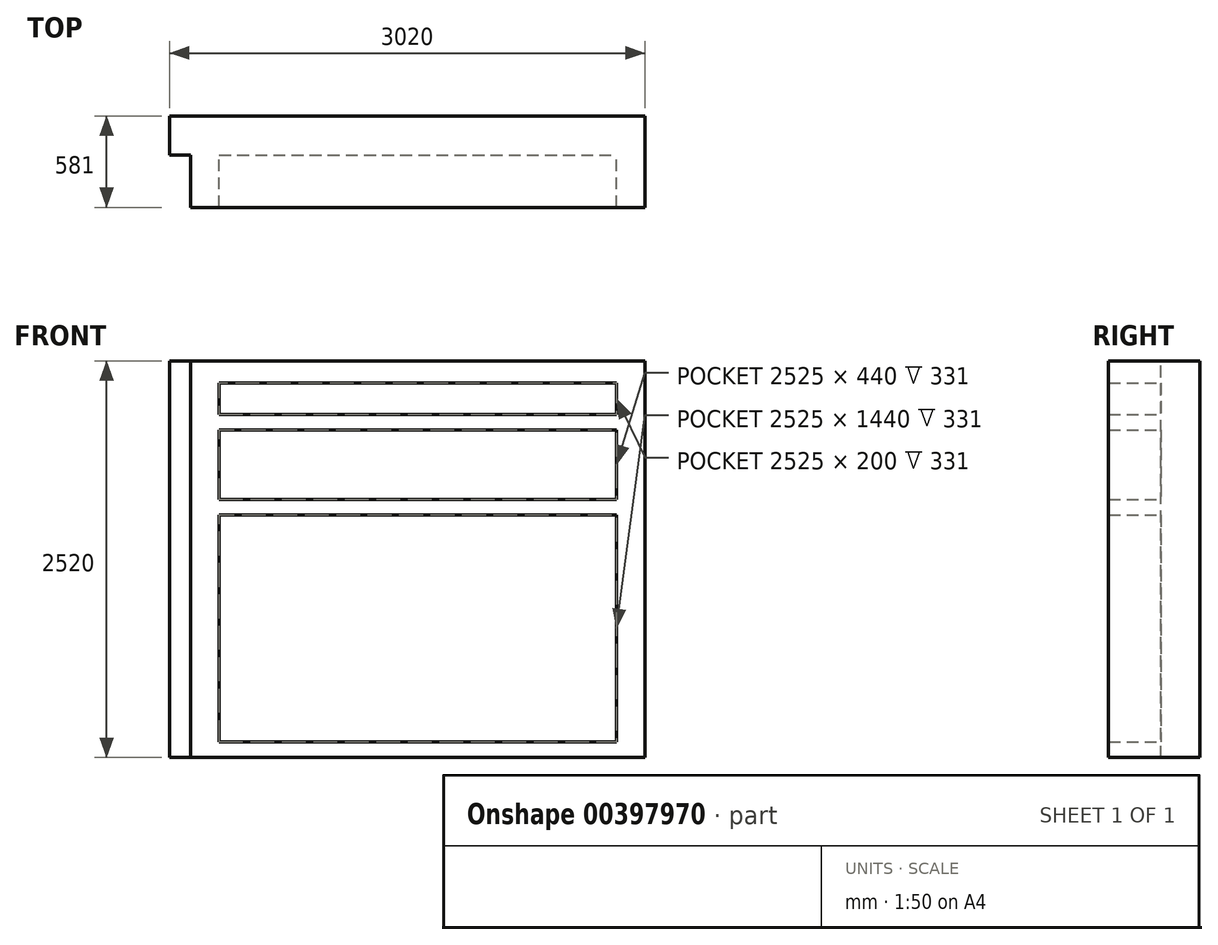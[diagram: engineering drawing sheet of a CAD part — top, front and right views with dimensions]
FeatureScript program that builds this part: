
annotation { "Feature Type Name" : "Feature", "Feature Type Description" : "" }
export const myFeature = defineFeature(function(context is Context, id is Id, definition is map)
    precondition{}
    {
        {
            var Q0;
            Q0=qCreatedBy(makeId("Front.planeOp"),FACE);
            var sketch = newSketch(context, id + "F0", { "sketchPlane" : qUnion([Q0])});
            skLineSegment(sketch, "E0.bottom", {"start": v(-1543.56, 0) * mm, "end": v(1476.44, 0) * mm});
            skLineSegment(sketch, "E0.top", {"start": v(-1543.56, 2520) * mm, "end": v(1476.44, 2520) * mm});
            skLineSegment(sketch, "E0.left", {"start": v(-1543.56, 0) * mm, "end": v(-1543.56, 2520) * mm});
            skLineSegment(sketch, "E0.right", {"start": v(1476.44, 0) * mm, "end": v(1476.44, 2520) * mm});
            skSolve(sketch);
        }
        {
            var Q0;
            Q0 = qSketchRegion(id + "F0", true);
            extrude(context, id + "F1", {"entities" : qUnion([Q0]), "depth" : 250 * mm});
        }
        {
            var Q0;
            Q0=makeQuery(id+"F1.opExtrude","CAP_FACE",FACE,{"disambiguationData":[OSD([sQuery(id+"F0.wireOp",EDGE,"E0.bottom"),sQuery(id+"F0.wireOp",EDGE,"E0.top"),sQuery(id+"F0.wireOp",EDGE,"E0.left"),sQuery(id+"F0.wireOp",EDGE,"E0.right")])],"isStart":false});
            var sketch = newSketch(context, id + "F2", { "sketchPlane" : qUnion([Q0])});
            skLineSegment(sketch, "E1.bottom", {"start": v(-1408.56, 2520) * mm, "end": v(-1228.56, 2520) * mm});
            skLineSegment(sketch, "E1.top", {"start": v(-1408.56, 0) * mm, "end": v(-1228.56, 0) * mm});
            skLineSegment(sketch, "E1.left", {"start": v(-1408.56, 2520) * mm, "end": v(-1408.56, 0) * mm});
            skLineSegment(sketch, "E1.right", {"start": v(-1228.56, 2520) * mm, "end": v(-1228.56, 0) * mm});
            skLineSegment(sketch, "E2.bottom", {"start": v(1476.44, 2520) * mm, "end": v(1296.44, 2520) * mm});
            skLineSegment(sketch, "E2.top", {"start": v(1476.44, 0) * mm, "end": v(1296.44, 0) * mm});
            skLineSegment(sketch, "E2.left", {"start": v(1476.44, 2520) * mm, "end": v(1476.44, 0) * mm});
            skLineSegment(sketch, "E2.right", {"start": v(1296.44, 2520) * mm, "end": v(1296.44, 0) * mm});
            skLineSegment(sketch, "E3.bottom", {"start": v(-1228.56, 2520) * mm, "end": v(1296.44, 2520) * mm});
            skLineSegment(sketch, "E3.top", {"start": v(-1228.56, 2380) * mm, "end": v(1296.44, 2380) * mm});
            skLineSegment(sketch, "E3.left", {"start": v(-1228.56, 2520) * mm, "end": v(-1228.56, 2380) * mm});
            skLineSegment(sketch, "E3.right", {"start": v(1296.44, 2520) * mm, "end": v(1296.44, 2380) * mm});
            skLineSegment(sketch, "E4.bottom", {"start": v(-1228.56, 100) * mm, "end": v(1296.44, 100) * mm});
            skLineSegment(sketch, "E4.top", {"start": v(-1228.56, 0) * mm, "end": v(1296.44, 0) * mm});
            skLineSegment(sketch, "E4.left", {"start": v(-1228.56, 100) * mm, "end": v(-1228.56, 0) * mm});
            skLineSegment(sketch, "E4.right", {"start": v(1296.44, 100) * mm, "end": v(1296.44, 0) * mm});
            skLineSegment(sketch, "E5.bottom", {"start": v(-1228.56, 1640) * mm, "end": v(1296.44, 1640) * mm});
            skLineSegment(sketch, "E5.top", {"start": v(-1228.56, 1540) * mm, "end": v(1296.44, 1540) * mm});
            skLineSegment(sketch, "E5.left", {"start": v(-1228.56, 1640) * mm, "end": v(-1228.56, 1540) * mm});
            skLineSegment(sketch, "E5.right", {"start": v(1296.44, 1640) * mm, "end": v(1296.44, 1540) * mm});
            skLineSegment(sketch, "E6.bottom", {"start": v(-1228.56, 2080) * mm, "end": v(1296.44, 2080) * mm});
            skLineSegment(sketch, "E6.top", {"start": v(-1228.56, 2180) * mm, "end": v(1296.44, 2180) * mm});
            skLineSegment(sketch, "E6.left", {"start": v(-1228.56, 2080) * mm, "end": v(-1228.56, 2180) * mm});
            skLineSegment(sketch, "E6.right", {"start": v(1296.44, 2080) * mm, "end": v(1296.44, 2180) * mm});
            skSolve(sketch);
        }
        {
            var Q0;
            Q0=makeQuery(id+"F2.imprint","IMPRINT",FACE,{"disambiguationData":[TD([[makeQuery(id+"F2.imprint","IMPRINT",EDGE,{"derivedFrom":sQuery(id+"F2.wireOp",EDGE,"E1.bottom")}),-1.0]])]});
            var Q1;
            Q1=makeQuery(id+"F2.imprint","IMPRINT",FACE,{"disambiguationData":[TD([[makeQuery(id+"F2.imprint","IMPRINT",EDGE,{"derivedFrom":sQuery(id+"F2.wireOp",EDGE,"E3.bottom")}),-1.0]])]});
            var Q2;
            Q2=makeQuery(id+"F2.imprint","IMPRINT",FACE,{"disambiguationData":[TD([[makeQuery(id+"F2.imprint","IMPRINT",EDGE,{"derivedFrom":sQuery(id+"F2.wireOp",EDGE,"E6.bottom")}),1.0]])]});
            var Q3;
            Q3=makeQuery(id+"F2.imprint","IMPRINT",FACE,{"disambiguationData":[TD([[makeQuery(id+"F2.imprint","IMPRINT",EDGE,{"derivedFrom":sQuery(id+"F2.wireOp",EDGE,"E5.bottom")}),-1.0]])]});
            var Q4;
            Q4=makeQuery(id+"F2.imprint","IMPRINT",FACE,{"disambiguationData":[TD([[makeQuery(id+"F2.imprint","IMPRINT",EDGE,{"derivedFrom":sQuery(id+"F2.wireOp",EDGE,"E4.bottom")}),-1.0]])]});
            var Q5;
            Q5=makeQuery(id+"F2.imprint","IMPRINT",FACE,{"disambiguationData":[TD([[makeQuery(id+"F2.imprint","IMPRINT",EDGE,{"derivedFrom":sQuery(id+"F2.wireOp",EDGE,"E2.bottom")}),-1.0]])]});
            extrude(context, id + "F3", {"entities" : qUnion([Q0, Q1, Q2, Q3, Q4, Q5]), "operationType" : NewBodyOperationType.ADD, "depth" : 331 * mm});
        }
    });
